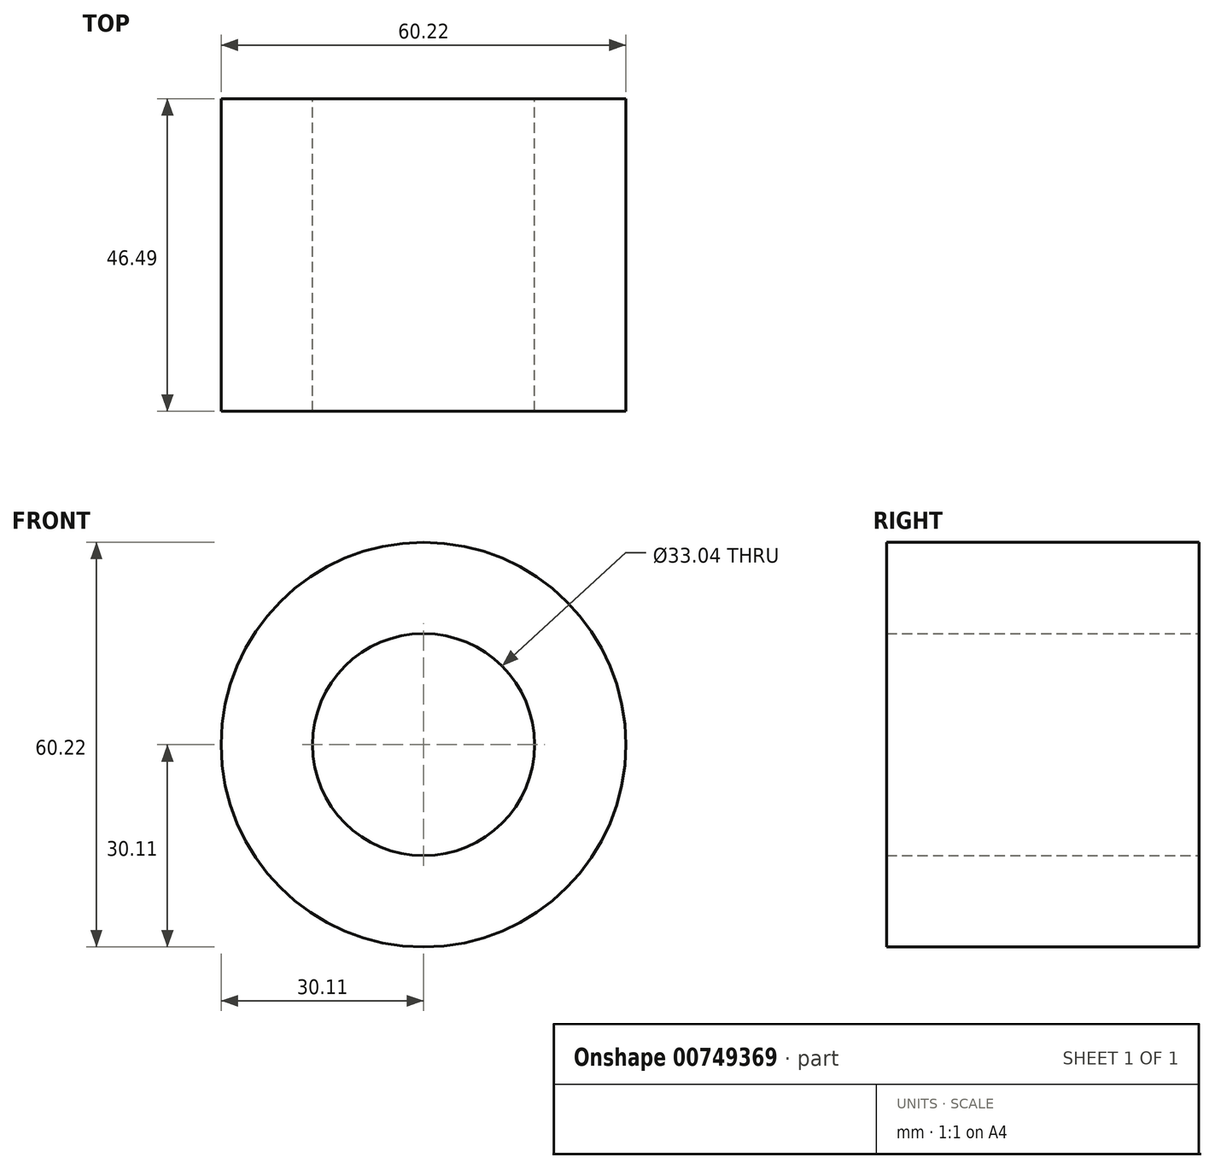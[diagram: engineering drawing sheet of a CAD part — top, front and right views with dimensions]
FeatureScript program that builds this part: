
annotation { "Feature Type Name" : "Feature", "Feature Type Description" : "" }
export const myFeature = defineFeature(function(context is Context, id is Id, definition is map)
    precondition{}
    {
        {
            var Q0;
            Q0=qCreatedBy(makeId("Front.planeOp"),FACE);
            var sketch = newSketch(context, id + "F0", { "sketchPlane" : qUnion([Q0])});
            skCircle(sketch, "E0", {"center": v(0, 0) * mm, "radius": 30.1 * mm});
            skCircle(sketch, "E1", {"center": v(0, 0) * mm, "radius": 16.52 * mm});
            skSolve(sketch);
        }
        {
            var Q0;
            Q0=makeQuery(id+"F0.imprint","IMPRINT",FACE,{"disambiguationData":[TD([[makeQuery(id+"F0.imprint","IMPRINT",EDGE,{"derivedFrom":sQuery(id+"F0.wireOp",EDGE,"E0")}),1.0]])]});
            extrude(context, id + "F1", {"entities" : qUnion([Q0]), "depth" : 46.5 * mm, "offsetDistance" : 25.4 * mm});
        }
    });
